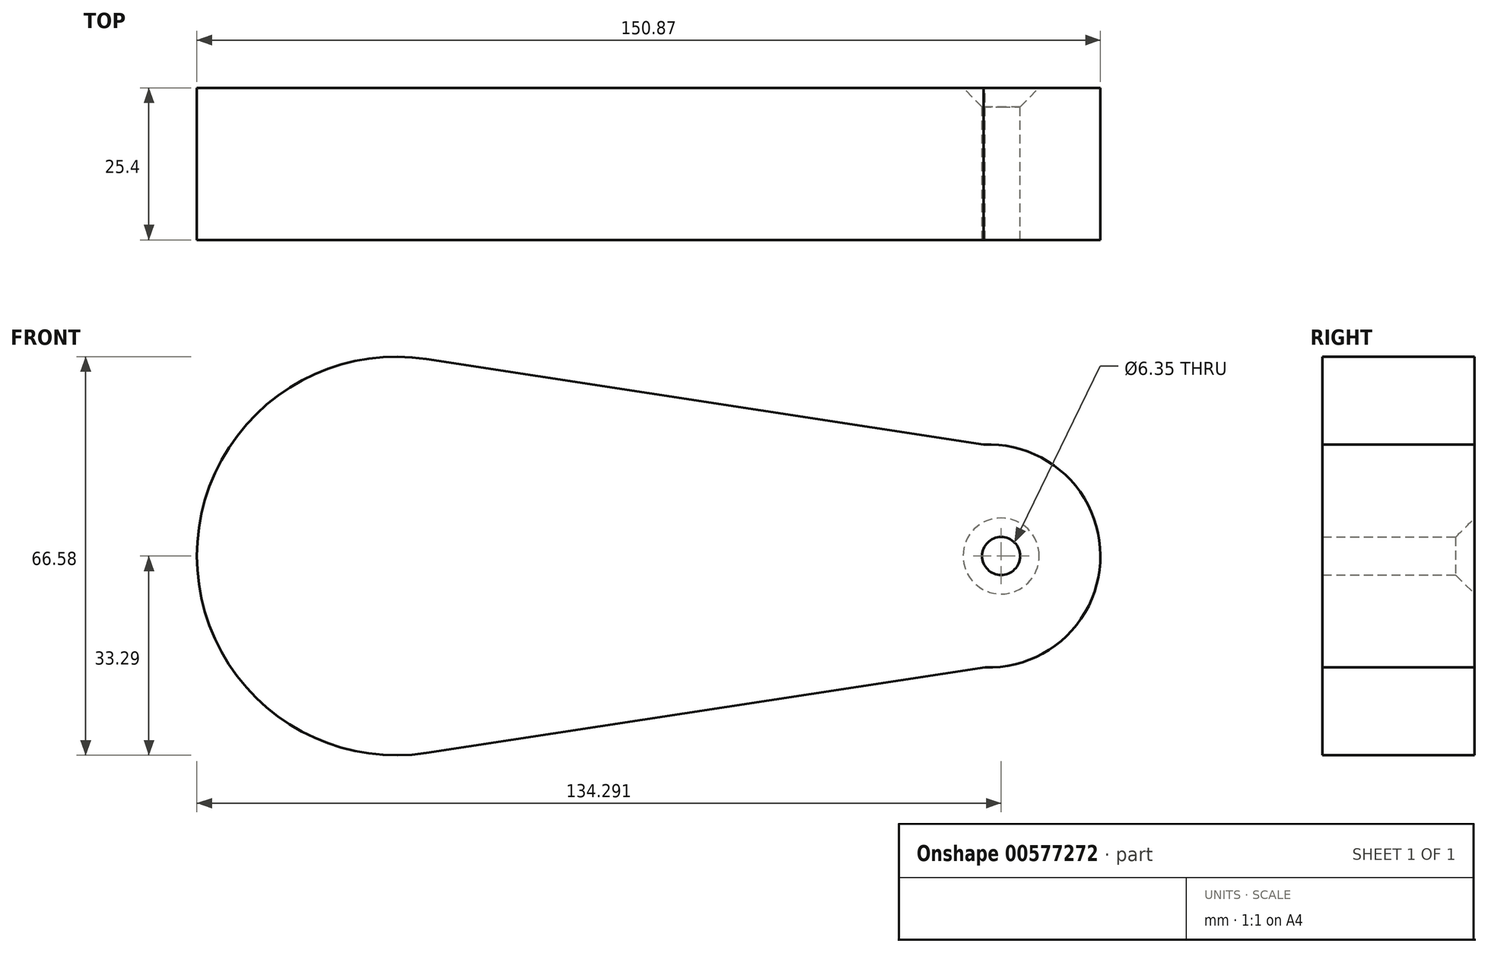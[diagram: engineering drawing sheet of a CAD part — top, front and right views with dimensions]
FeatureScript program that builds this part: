
annotation { "Feature Type Name" : "Feature", "Feature Type Description" : "" }
export const myFeature = defineFeature(function(context is Context, id is Id, definition is map)
    precondition{}
    {
        {
            var Q0;
            Q0=qCreatedBy(makeId("Front.planeOp"),FACE);
            var sketch = newSketch(context, id + "F0", { "sketchPlane" : qUnion([Q0])});
            skCircle(sketch, "E0", {"center": v(0, 0) * mm, "radius": 33.29 * mm});
            skCircle(sketch, "E1", {"center": v(98.97, 0) * mm, "radius": 18.61 * mm});
            skLineSegment(sketch, "E2", {"start": v(98.04, 18.59) * mm, "end": v(5.06, 32.9) * mm});
            skLineSegment(sketch, "E3", {"start": v(98.33, -18.6) * mm, "end": v(5.04, -32.9) * mm});
            skSolve(sketch);
        }
        {
            var Q0;
            Q0 = qSketchRegion(id + "F0", true);
            extrude(context, id + "F1", {"entities" : qUnion([Q0]), "depth" : 25.4 * mm, "offsetDistance" : 25.4 * mm});
        }
        {
            var Q0;
            Q0=qCreatedBy(makeId("Front.planeOp"),FACE);
            var sketch = newSketch(context, id + "F2", { "sketchPlane" : qUnion([Q0])});
            skCircle(sketch, "E4", {"center": v(0, 0) * mm, "radius": 15.41 * mm});
            skCircle(sketch, "E5", {"center": v(101, 0) * mm, "radius": 8.52 * mm});
            skSolve(sketch);
        }
        {
            var Q0;
            Q0=sQuery(id+"F2.wireOp",VERTEX,"E5.center");
            var Q1;
            Q1=makeQuery(id+"F1.opExtrude","SWEPT_BODY",BODY,{"disambiguationData":[OSD([sQuery(id+"F0.wireOp",EDGE,"E0"),sQuery(id+"F0.wireOp",EDGE,"E1"),sQuery(id+"F0.wireOp",EDGE,"E2"),sQuery(id+"F0.wireOp",EDGE,"E3")])]});
            hole(context, id + "F3", {"style" : HoleStyle.C_SINK, "endStyle" : HoleEndStyle.THROUGH, "oppositeDirection" : true, "holeDiameter" : 6.35 * mm, "cSinkDiameter" : 12.7 * mm, "cSinkAngle" : 90 * degree, "isTappedThrough" : true, "tappedDepth" : 12.7 * mm, "tapClearance" : 3, "locations" : qUnion([Q0]), "scope" : qUnion([Q1])});
        }
    });
